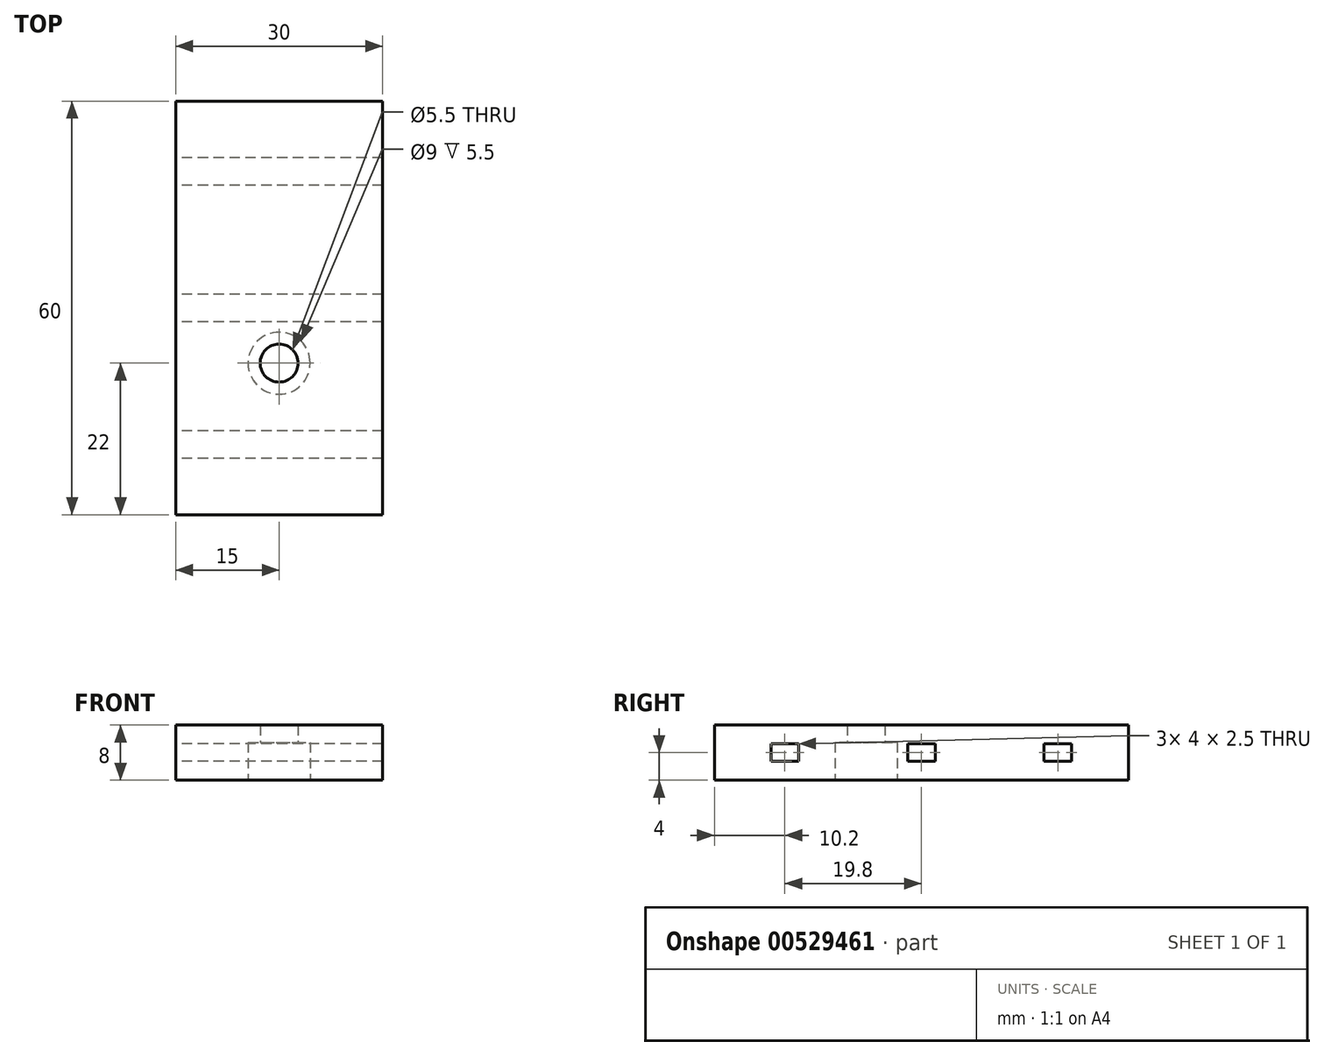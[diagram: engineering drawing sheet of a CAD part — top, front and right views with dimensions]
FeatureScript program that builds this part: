
annotation { "Feature Type Name" : "Feature", "Feature Type Description" : "" }
export const myFeature = defineFeature(function(context is Context, id is Id, definition is map)
    precondition{}
    {
        {
            var Q0;
            Q0=qCreatedBy(makeId("Top.planeOp"),FACE);
            var sketch = newSketch(context, id + "F0", { "sketchPlane" : qUnion([Q0])});
            skLineSegment(sketch, "E0.bottom", {"start": v(15, 30) * mm, "end": v(-15, 30) * mm});
            skLineSegment(sketch, "E0.top", {"start": v(15, -30) * mm, "end": v(-15, -30) * mm});
            skLineSegment(sketch, "E0.left", {"start": v(15, 30) * mm, "end": v(15, -30) * mm});
            skLineSegment(sketch, "E0.right", {"start": v(-15, 30) * mm, "end": v(-15, -30) * mm});
            skPoint(sketch, "E0.middle", {"position": v(0, 0) * mm});
            skLineSegment(sketch, "E1", {"start": v(0, -30) * mm, "end": v(0, 30) * mm, "construction": true});
            skPoint(sketch, "E2", {"position": v(0, -8) * mm});
            skSolve(sketch);
        }
        {
            var Q0;
            Q0=makeQuery(id+"F0.imprint","IMPRINT",FACE,{"disambiguationData":[TD([[makeQuery(id+"F0.imprint","IMPRINT",EDGE,{"derivedFrom":sQuery(id+"F0.wireOp",EDGE,"E0.bottom")}),1.0]])]});
            extrude(context, id + "F1", {"entities" : qUnion([Q0]), "depth" : 8 * mm, "offsetDistance" : 25 * mm});
        }
        {
            var Q0;
            Q0=sQuery(id+"F0.wireOp",VERTEX,"E2");
            var Q1;
            Q1=makeQuery(id+"F1.opExtrude","SWEPT_BODY",BODY,{"disambiguationData":[OSD([sQuery(id+"F0.wireOp",EDGE,"E0.bottom"),sQuery(id+"F0.wireOp",EDGE,"E0.top"),sQuery(id+"F0.wireOp",EDGE,"E0.left"),sQuery(id+"F0.wireOp",EDGE,"E0.right")])]});
            hole(context, id + "F2", {"style" : HoleStyle.C_BORE, "endStyle" : HoleEndStyle.BLIND, "oppositeDirection" : true, "holeDiameter" : 5.5 * mm, "cBoreDiameter" : 9 * mm, "cBoreDepth" : 5.5 * mm, "majorDiameter" : 5 * mm, "holeDepth" : 30 * mm, "isTappedThrough" : true, "tappedDepth" : 10.5 * mm, "tapClearance" : 3, "locations" : qUnion([Q0]), "scope" : qUnion([Q1])});
        }
        {
            var Q0;
            Q0=makeQuery(id+"F1.opExtrude","SWEPT_FACE",FACE,{"disambiguationData":[OSD([sQuery(id+"F0.wireOp",EDGE,"E0.right")])]});
            var sketch = newSketch(context, id + "F3", { "sketchPlane" : qUnion([Q0])});
            skLineSegment(sketch, "E3.bottom", {"start": v(-17.8, 5.25) * mm, "end": v(-21.8, 5.25) * mm});
            skLineSegment(sketch, "E3.top", {"start": v(-17.8, 2.75) * mm, "end": v(-21.8, 2.75) * mm});
            skLineSegment(sketch, "E3.left", {"start": v(-17.8, 5.25) * mm, "end": v(-17.8, 2.75) * mm});
            skLineSegment(sketch, "E3.right", {"start": v(-21.8, 5.25) * mm, "end": v(-21.8, 2.75) * mm});
            skPoint(sketch, "E3.middle", {"position": v(-19.8, 4) * mm});
            skLineSegment(sketch, "E4.1.0.0", {"start": v(2, 5.25) * mm, "end": v(2, 2.75) * mm});
            skLineSegment(sketch, "E4.1.0.1", {"start": v(-2, 5.25) * mm, "end": v(-2, 2.75) * mm});
            skLineSegment(sketch, "E4.1.0.2", {"start": v(2, 5.25) * mm, "end": v(-2, 5.25) * mm});
            skLineSegment(sketch, "E4.1.0.3", {"start": v(2, 2.75) * mm, "end": v(-2, 2.75) * mm});
            skPoint(sketch, "E4.1.0.4", {"position": v(0, 4) * mm});
            skLineSegment(sketch, "E4.2.0.0", {"start": v(21.8, 5.25) * mm, "end": v(21.8, 2.75) * mm});
            skLineSegment(sketch, "E4.2.0.1", {"start": v(17.8, 5.25) * mm, "end": v(17.8, 2.75) * mm});
            skLineSegment(sketch, "E4.2.0.2", {"start": v(21.8, 5.25) * mm, "end": v(17.8, 5.25) * mm});
            skLineSegment(sketch, "E4.2.0.3", {"start": v(21.8, 2.75) * mm, "end": v(17.8, 2.75) * mm});
            skPoint(sketch, "E4.2.0.4", {"position": v(19.8, 4) * mm});
            skLineSegment(sketch, "E4.direction1", {"start": v(-21.8, 2.75) * mm, "end": v(-2, 2.75) * mm, "construction": true});
            skLineSegment(sketch, "E5", {"start": v(0, 0) * mm, "end": v(0, 8) * mm, "construction": true});
            skSolve(sketch);
        }
        {
            var Q0;
            Q0 = qSketchRegion(id + "F3", true);
            extrude(context, id + "F4", {"entities" : qUnion([Q0]), "operationType" : NewBodyOperationType.REMOVE, "endBound" : BoundingType.THROUGH_ALL, "oppositeDirection" : true, "depth" : 25 * mm, "offsetDistance" : 25 * mm});
        }
    });
